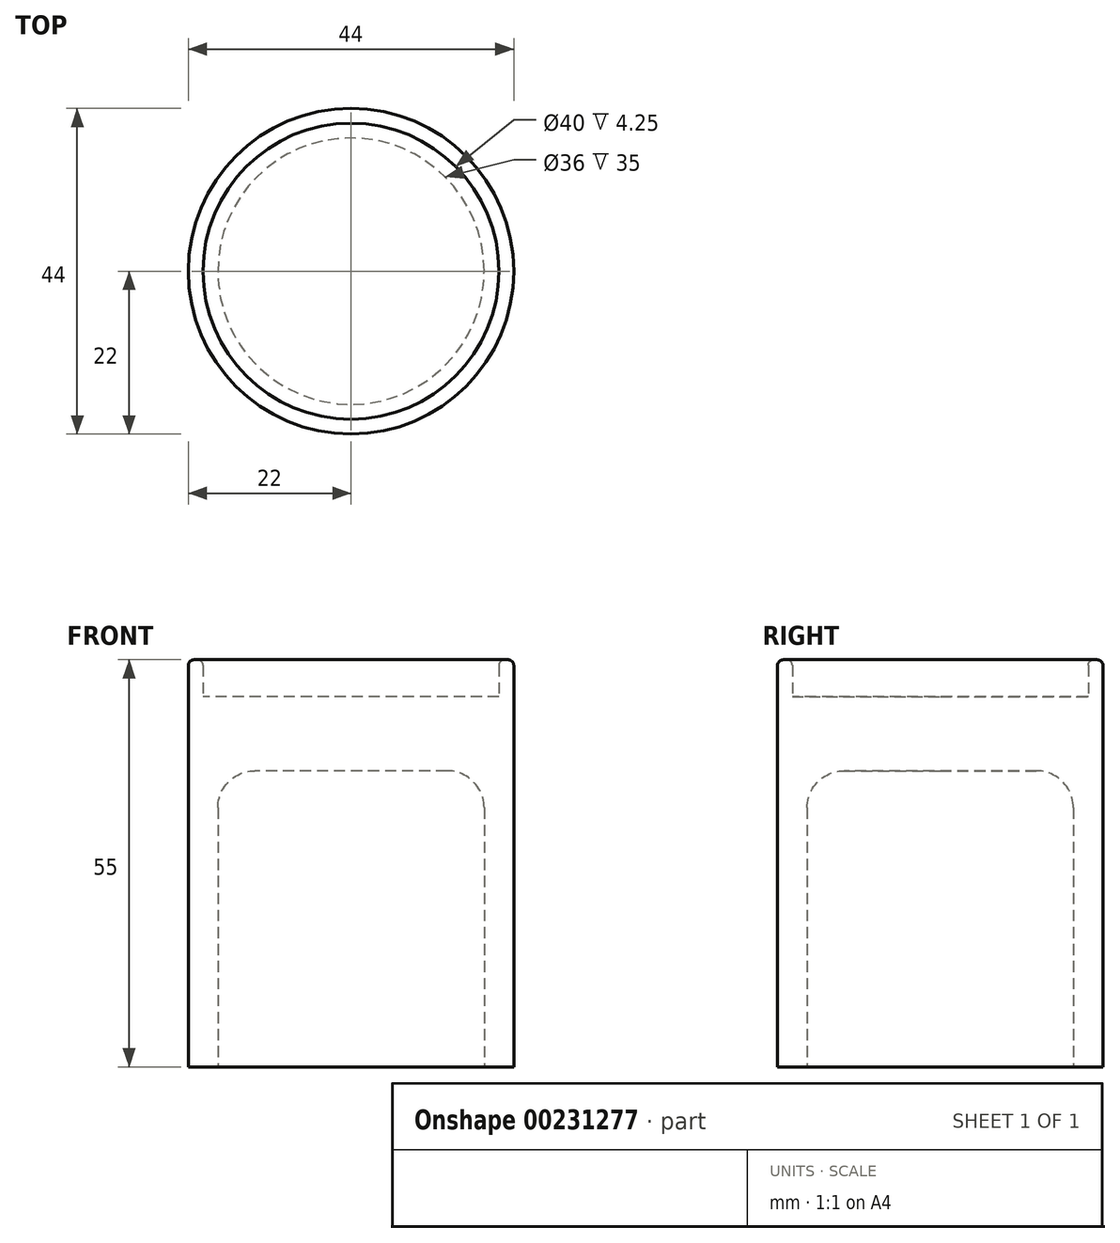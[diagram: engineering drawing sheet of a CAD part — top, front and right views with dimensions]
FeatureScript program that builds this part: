
annotation { "Feature Type Name" : "Feature", "Feature Type Description" : "" }
export const myFeature = defineFeature(function(context is Context, id is Id, definition is map)
    precondition{}
    {
        {
            var Q0;
            Q0=qCreatedBy(makeId("Top.planeOp"),FACE);
            var sketch = newSketch(context, id + "F0", { "sketchPlane" : qUnion([Q0])});
            skCircle(sketch, "E0", {"center": v(0, 0) * mm, "radius": 20 * mm});
            skCircle(sketch, "E1", {"center": v(0, 0) * mm, "radius": 22 * mm});
            skCircle(sketch, "E2", {"center": v(0, 0) * mm, "radius": 18 * mm});
            skSolve(sketch);
        }
        {
            var Q0;
            Q0=makeQuery(id+"F0.imprint","IMPRINT",FACE,{"disambiguationData":[TD([[makeQuery(id+"F0.imprint","IMPRINT",EDGE,{"derivedFrom":sQuery(id+"F0.wireOp",EDGE,"E0")}),1.0]])]});
            var Q1;
            Q1=makeQuery(id+"F0.imprint","IMPRINT",FACE,{"disambiguationData":[TD([[makeQuery(id+"F0.imprint","IMPRINT",EDGE,{"derivedFrom":sQuery(id+"F0.wireOp",EDGE,"E2")}),1.0]])]});
            extrude(context, id + "F1", {"entities" : qUnion([Q0, Q1]), "depth" : 50 * mm});
        }
        {
            var Q0;
            Q0 = qSketchRegion(id + "F0", true);
            extrude(context, id + "F2", {"entities" : qUnion([Q0]), "operationType" : NewBodyOperationType.ADD, "depth" : 55 * mm});
        }
        {
            var Q0;
            Q0=makeQuery(id+"F0.imprint","IMPRINT",FACE,{"disambiguationData":[TD([[makeQuery(id+"F0.imprint","IMPRINT",EDGE,{"derivedFrom":sQuery(id+"F0.wireOp",EDGE,"E2")}),1.0]])]});
            extrude(context, id + "F3", {"entities" : qUnion([Q0]), "operationType" : NewBodyOperationType.REMOVE, "depth" : 40 * mm});
        }
        {
            var Q0;
            Q0=makeQuery(id+"F2.opExtrude","CAP_EDGE",EDGE,{"disambiguationData":[OSD([sQuery(id+"F0.wireOp",EDGE,"E0")])],"isStart":false});
            fillet(context, id + "F4", {"entities" : qUnion([Q0]), "radius" : 0.75 * mm, "tangentPropagation" : true, "allowEdgeOverflow" : false});
        }
        {
            var Q0;
            Q0=makeQuery(id+"F2.opExtrude","CAP_EDGE",EDGE,{"disambiguationData":[OSD([sQuery(id+"F0.wireOp",EDGE,"E1")])],"isStart":false});
            fillet(context, id + "F5", {"entities" : qUnion([Q0]), "radius" : 0.75 * mm, "tangentPropagation" : true, "allowEdgeOverflow" : false});
        }
        {
            var Q0;
            Q0=makeQuery(id+"F3.boolean.opBoolean","COPY",EDGE,{"derivedFrom":makeQuery(id+"F3.opExtrude","CAP_EDGE",EDGE,{"disambiguationData":[OSD([sQuery(id+"F0.wireOp",EDGE,"E2")])],"isStart":false})});
            fillet(context, id + "F6", {"entities" : qUnion([Q0]), "radius" : 5 * mm, "tangentPropagation" : true, "allowEdgeOverflow" : false});
        }
    });
